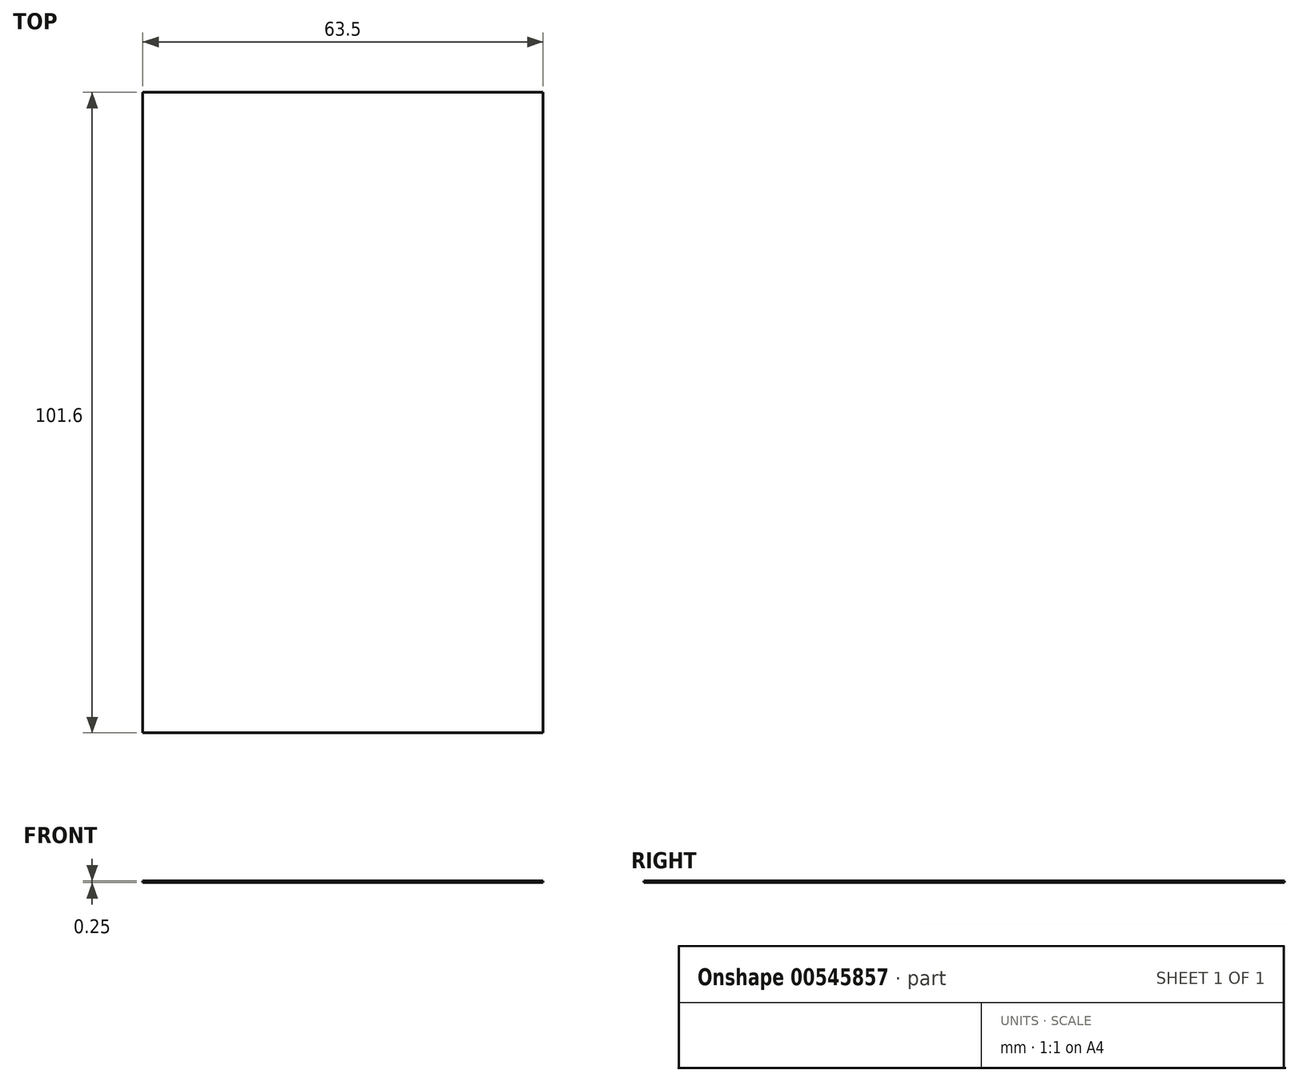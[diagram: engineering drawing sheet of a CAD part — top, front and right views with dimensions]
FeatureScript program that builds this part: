
annotation { "Feature Type Name" : "Feature", "Feature Type Description" : "" }
export const myFeature = defineFeature(function(context is Context, id is Id, definition is map)
    precondition{}
    {
        {
            var Q0;
            Q0=qCreatedBy(makeId("Top.planeOp"),FACE);
            var sketch = newSketch(context, id + "F0", { "sketchPlane" : qUnion([Q0])});
            skLineSegment(sketch, "E0.bottom", {"start": v(-35.36, -50.8) * mm, "end": v(28.14, -50.8) * mm});
            skLineSegment(sketch, "E0.top", {"start": v(-35.36, 50.8) * mm, "end": v(28.14, 50.8) * mm});
            skLineSegment(sketch, "E0.left", {"start": v(-35.36, -50.8) * mm, "end": v(-35.36, 50.8) * mm});
            skLineSegment(sketch, "E0.right", {"start": v(28.14, -50.8) * mm, "end": v(28.14, 50.8) * mm});
            skSolve(sketch);
        }
        {
            var Q0;
            Q0=makeQuery(id+"F0.imprint","IMPRINT",FACE,{"disambiguationData":[TD([[makeQuery(id+"F0.imprint","IMPRINT",EDGE,{"derivedFrom":sQuery(id+"F0.wireOp",EDGE,"E0.bottom")}),1.0]])]});
            extrude(context, id + "F1", {"entities" : qUnion([Q0]), "depth" : 0.25 * mm, "offsetDistance" : 25.4 * mm});
        }
    });
